# Revit family: Zurn_One-System-Zurn-ZWC1STM
name_source: partatom
category: Plumbing Fixtures
units: mm (PartAtom-declared; Revit-internal decimal feet)

## family parameters
Cut with Voids When Loaded = No
Host = Face
Maintain Annotation Orientation = No
OmniClass Number = 23.45.05.00
OmniClass Title = Sanitary Equipment
Part Type = Normal
Room Calculation Point = No
Round Connector Dimension = Use Diameter
Shared = No

## types (1)
- Z.WC1.S.TM (Wall Hung Zurn One Toilet System with Top Mount 1.1 GPF Battery Powered Sensor Flush Valve)
    Accessory 1 = Z5977-NEO
    Accessory 2 = Z5610-NUT-EXT-KIT
    Assembly Code = D2010.60
    CW Connection = Yes
    CWFU = 0
    Default Elevation = 48 "
    Description = Zurn One Sensor Wall Hung Toilet System with 1.1 GPF EcoVantage® Battery Powered Flush Valve
    Fixture  Material = Vitreous China - Zurn - White
    Fixture Number = Z5615-BWL
    Flush Valve Material = Chrome-Plated Brass - Zurn - Polished
    Flush Valve Number = ZER6000AV-ONE-TM
    Flush rate (GPF) = 1.1 GPF
    HW Connection = No
    HWFU = 0
    Inlet Connection Size (inch) = 1 "
    Manufacturer = Zurn Water, LLC
    Manufacturer Brand = Zurn
    Mode of Installation = Wall Mounted
    Model = Z.WC1.S.TM
    Modified Date = 07/03/2025
    Outlet Connection Size (inch) = 1 "
    Product Documentation Link = https://files.zurn.com
    Product Page URL = https://www.zurn.com
    Product data URL = https://bimobject.com
    Seat Number = Z5955SS-EL
    URL = https://www.zurn.com
    Vent Connection = No
    WFU = 0
    Waste Connection = Yes

## geometry (parser evidence)
native form markers: Blend x8, Sweep x30
no freeform markers — native parametric forms only
